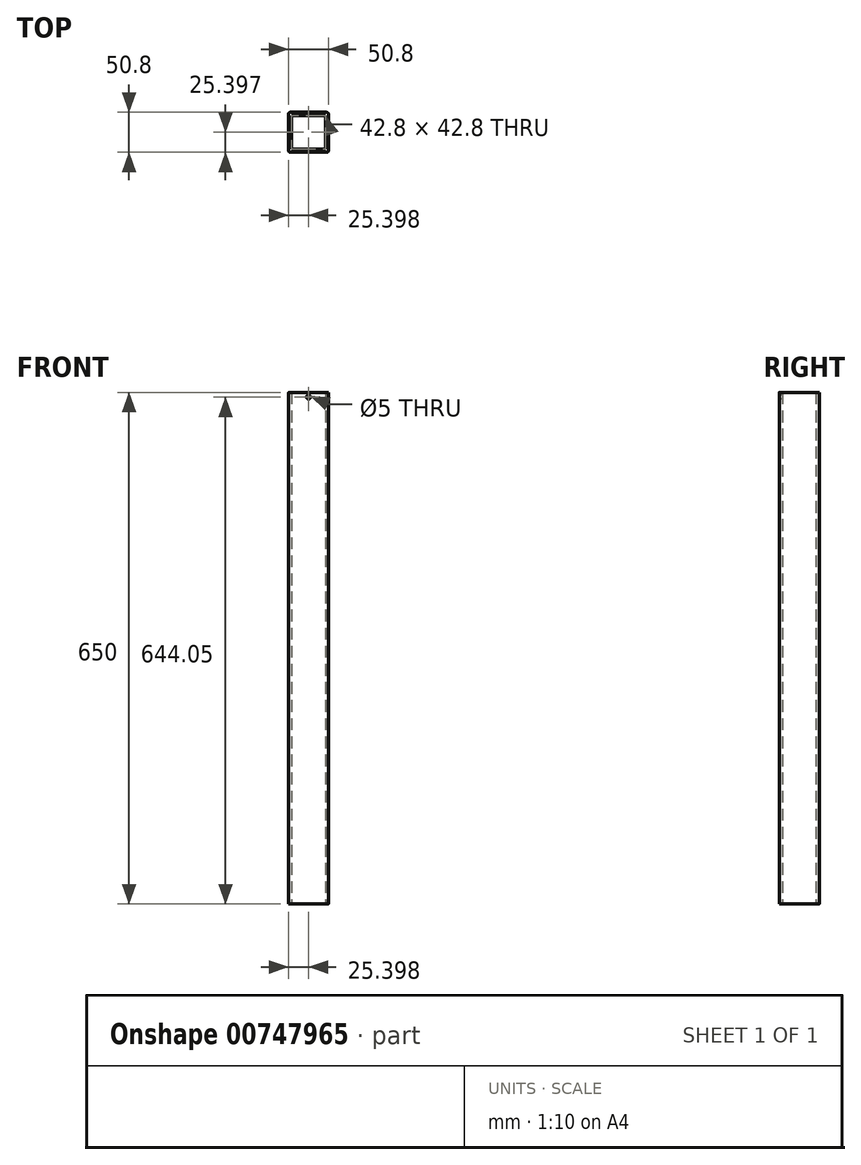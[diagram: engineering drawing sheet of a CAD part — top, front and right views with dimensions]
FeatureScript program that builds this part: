
annotation { "Feature Type Name" : "Feature", "Feature Type Description" : "" }
export const myFeature = defineFeature(function(context is Context, id is Id, definition is map)
    precondition{}
    {
        {
            var Q0;
            Q0=qCreatedBy(makeId("Top.planeOp"),FACE);
            var sketch = newSketch(context, id + "F0", { "sketchPlane" : qUnion([Q0])});
            skLineSegment(sketch, "E0.bottom", {"start": v(-46.11, 27.05) * mm, "end": v(-0.31, 27.05) * mm});
            skLineSegment(sketch, "E0.top", {"start": v(-46.11, -23.75) * mm, "end": v(-0.31, -23.75) * mm});
            skLineSegment(sketch, "E0.left", {"start": v(-48.61, 24.55) * mm, "end": v(-48.61, -21.25) * mm});
            skLineSegment(sketch, "E0.right", {"start": v(2.19, 24.55) * mm, "end": v(2.19, -21.25) * mm});
            skPoint(sketch, "E1.visualSharp", {"position": v(-48.61, 27.05) * mm});
            skArc(sketch, "E1.filletArc", {"start": v(-46.11, 27.05) * mm, "mid": v(-47.88, 26.31) * mm, "end": v(-48.61, 24.55) * mm});
            skPoint(sketch, "E2.visualSharp", {"position": v(-48.61, -23.75) * mm});
            skArc(sketch, "E2.filletArc", {"start": v(-48.61, -21.25) * mm, "mid": v(-47.88, -23.02) * mm, "end": v(-46.11, -23.75) * mm});
            skPoint(sketch, "E3.visualSharp", {"position": v(2.19, -23.75) * mm});
            skArc(sketch, "E3.filletArc", {"start": v(-0.31, -23.75) * mm, "mid": v(1.46, -23.02) * mm, "end": v(2.19, -21.25) * mm});
            skPoint(sketch, "E4.visualSharp", {"position": v(2.19, 27.05) * mm});
            skArc(sketch, "E4.filletArc", {"start": v(2.19, 24.55) * mm, "mid": v(1.46, 26.31) * mm, "end": v(-0.31, 27.05) * mm});
            skLineSegment(sketch, "E5.1", {"start": v(-44.61, 23.05) * mm, "end": v(-44.61, -19.75) * mm});
            skLineSegment(sketch, "E5.2", {"start": v(-44.61, 23.05) * mm, "end": v(-1.81, 23.05) * mm});
            skLineSegment(sketch, "E5.5", {"start": v(-1.81, 23.05) * mm, "end": v(-1.81, -19.75) * mm});
            skLineSegment(sketch, "E5.7", {"start": v(-44.61, -19.75) * mm, "end": v(-1.81, -19.75) * mm});
            skLineSegment(sketch, "E6", {"start": v(2.19, 27.05) * mm, "end": v(-48.61, -23.75) * mm, "construction": true});
            skSolve(sketch);
        }
        {
            var Q0;
            Q0=makeQuery(id+"F0.imprint","IMPRINT",FACE,{"disambiguationData":[TD([[makeQuery(id+"F0.imprint","IMPRINT",EDGE,{"derivedFrom":sQuery(id+"F0.wireOp",EDGE,"E0.bottom")}),-1.0]])]});
            extrude(context, id + "F1", {"entities" : qUnion([Q0]), "depth" : 650 * mm, "offsetDistance" : 25 * mm});
        }
        {
            var Q0;
            Q0=makeQuery(id+"F1.opExtrude","SWEPT_FACE",FACE,{"disambiguationData":[OSD([sQuery(id+"F0.wireOp",EDGE,"E0.top")])]});
            var sketch = newSketch(context, id + "F2", { "sketchPlane" : qUnion([Q0])});
            skPoint(sketch, "E7", {"position": v(-23.21, 644.05) * mm});
            skSolve(sketch);
        }
        {
            var Q0;
            Q0=sQuery(id+"F2.wireOp",VERTEX,"E7");
            var Q1;
            Q1=makeQuery(id+"F1.opExtrude","SWEPT_BODY",BODY,{"disambiguationData":[OSD([sQuery(id+"F0.wireOp",EDGE,"E0.bottom"),sQuery(id+"F0.wireOp",EDGE,"E0.top"),sQuery(id+"F0.wireOp",EDGE,"E0.left"),sQuery(id+"F0.wireOp",EDGE,"E0.right"),sQuery(id+"F0.wireOp",EDGE,"E1.filletArc"),sQuery(id+"F0.wireOp",EDGE,"E2.filletArc"),sQuery(id+"F0.wireOp",EDGE,"E3.filletArc"),sQuery(id+"F0.wireOp",EDGE,"E4.filletArc"),sQuery(id+"F0.wireOp",EDGE,"E5.0"),sQuery(id+"F0.wireOp",EDGE,"E5.1"),sQuery(id+"F0.wireOp",EDGE,"E5.2"),sQuery(id+"F0.wireOp",EDGE,"E5.3"),sQuery(id+"F0.wireOp",EDGE,"E5.4"),sQuery(id+"F0.wireOp",EDGE,"E5.5"),sQuery(id+"F0.wireOp",EDGE,"E5.6"),sQuery(id+"F0.wireOp",EDGE,"E5.7")])]});
            hole(context, id + "F3", {"style" : HoleStyle.SIMPLE, "endStyle" : HoleEndStyle.BLIND, "standardTappedOrClearance" : lookupTablePath({ "standard" : "ISO", "engagement" : "75%", "pitch" : "1 mm", "size" : "M6", "type" : "Tapped" }), "standardBlindInLast" : lookupTablePath({ "standard" : "ISO", "engagement" : "75%", "pitch" : "1 mm", "size" : "M6", "type" : "Tapped" }), "holeDiameter" : 5 * mm, "majorDiameter" : 6 * mm, "showTappedDepth" : true, "holeDepth" : 15 * mm, "isTappedThrough" : true, "tappedDepth" : 12 * mm, "tapClearance" : 3, "startFromSketch" : true, "locations" : qUnion([Q0]), "scope" : qUnion([Q1])});
        }
        {
            var Q0;
            Q0=makeQuery(id+"F1.opExtrude","CAP_FACE",FACE,{"disambiguationData":[OSD([sQuery(id+"F0.wireOp",EDGE,"E0.bottom"),sQuery(id+"F0.wireOp",EDGE,"E0.top"),sQuery(id+"F0.wireOp",EDGE,"E0.left"),sQuery(id+"F0.wireOp",EDGE,"E0.right"),sQuery(id+"F0.wireOp",EDGE,"E1.filletArc"),sQuery(id+"F0.wireOp",EDGE,"E2.filletArc"),sQuery(id+"F0.wireOp",EDGE,"E3.filletArc"),sQuery(id+"F0.wireOp",EDGE,"E4.filletArc"),sQuery(id+"F0.wireOp",EDGE,"E5.0"),sQuery(id+"F0.wireOp",EDGE,"E5.1"),sQuery(id+"F0.wireOp",EDGE,"E5.2"),sQuery(id+"F0.wireOp",EDGE,"E5.3"),sQuery(id+"F0.wireOp",EDGE,"E5.4"),sQuery(id+"F0.wireOp",EDGE,"E5.5"),sQuery(id+"F0.wireOp",EDGE,"E5.6"),sQuery(id+"F0.wireOp",EDGE,"E5.7")])],"isStart":false});
            var sketch = newSketch(context, id + "F4", { "sketchPlane" : qUnion([Q0])});
            skLineSegment(sketch, "E8", {"start": v(1.46, 26.31) * mm, "end": v(-47.88, -23.02) * mm, "construction": true});
            skSolve(sketch);
        }
        {
            var Q0;
            Q0=sQuery(id+"F4.wireOp",EDGE,"E8");
            var Q1;
            Q1=sQuery(id+"F0.wireOp",EDGE,"E6");
            cPlane(context, id + "F5", {"entities" : qUnion([Q0, Q1]), "cplaneType" : CPlaneType.LINE_ANGLE, "offset" : 25 * mm, "angle" : 0 * degree, "width" : 150 * mm, "height" : 150 * mm});
        }
        {
            var Q0;
            Q0=qCreatedBy(id+"F5.planeOp",FACE);
            var sketch = newSketch(context, id + "F6", { "sketchPlane" : qUnion([Q0])});
            skLineSegment(sketch, "E9.0", {"start": v(19.64, 650) * mm, "end": v(-50.13, 650) * mm, "construction": true});
            skLineSegment(sketch, "E10.0", {"start": v(20.67, 0) * mm, "end": v(-51.17, 0) * mm, "construction": true});
            skLineSegment(sketch, "E11", {"start": v(-15.25, 650) * mm, "end": v(-15.25, 0) * mm});
            skSolve(sketch);
        }
    });
